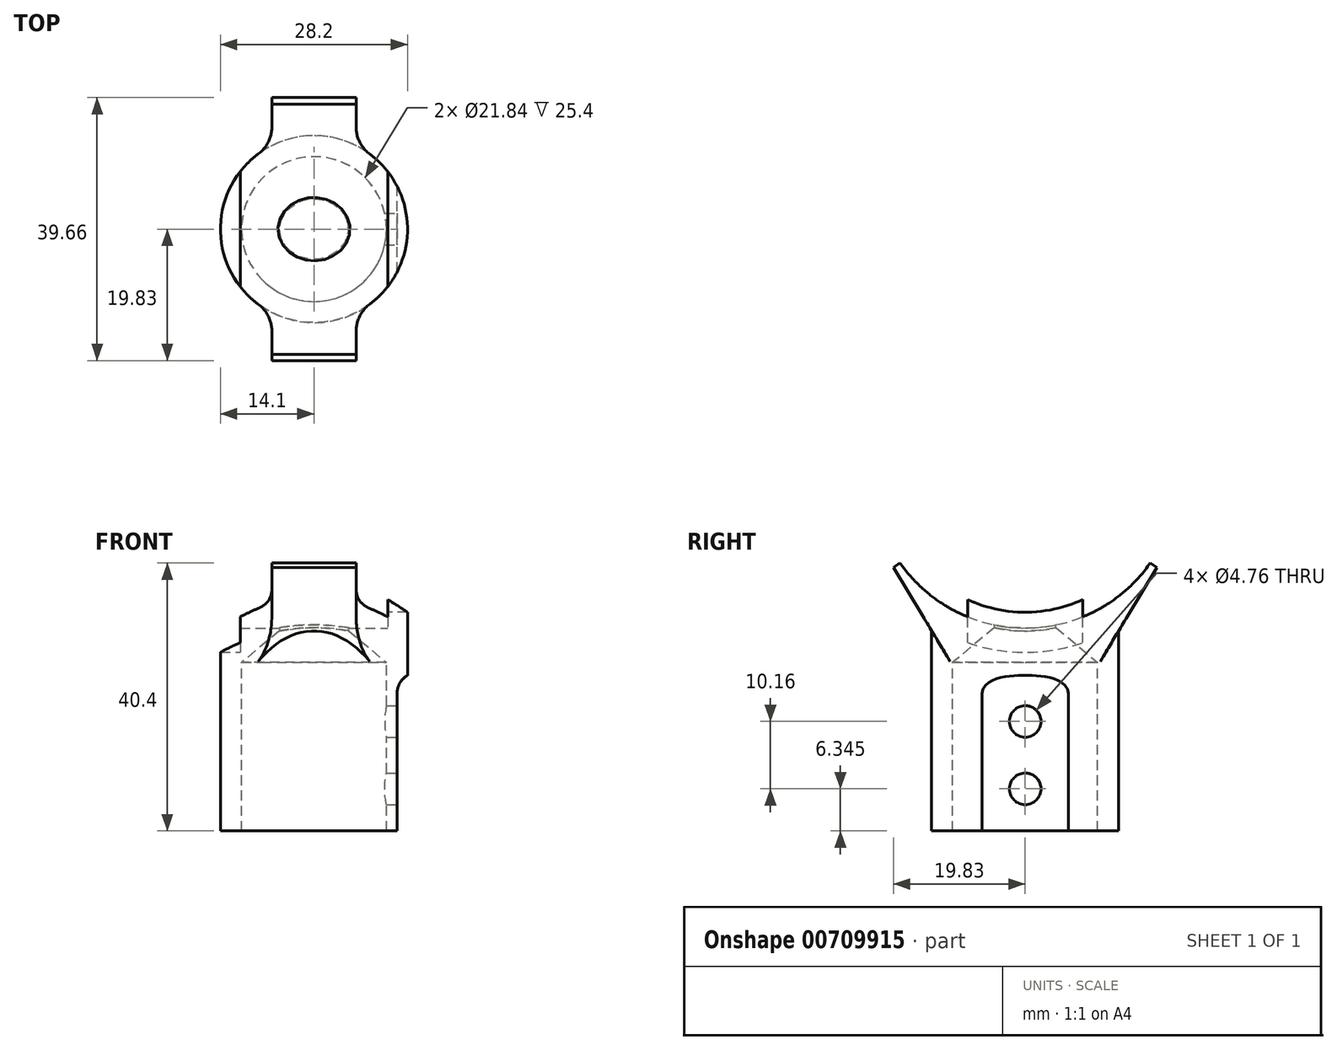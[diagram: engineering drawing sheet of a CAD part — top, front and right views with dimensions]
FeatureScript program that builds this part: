
annotation { "Feature Type Name" : "Feature", "Feature Type Description" : "" }
export const myFeature = defineFeature(function(context is Context, id is Id, definition is map)
    precondition{}
    {
        {
            var Q0;
            Q0=qCreatedBy(makeId("Front.planeOp"),FACE);
            var sketch = newSketch(context, id + "F0", { "sketchPlane" : qUnion([Q0])});
            skLineSegment(sketch, "E0", {"start": v(0, 0) * mm, "end": v(-10.92, -9.16) * mm});
            skLineSegment(sketch, "E1", {"start": v(-10.92, -9.16) * mm, "end": v(-10.92, -34.56) * mm});
            skLineSegment(sketch, "E2", {"start": v(0, 0) * mm, "end": v(0, -71.28) * mm, "construction": true});
            skLineSegment(sketch, "E3", {"start": v(-10.92, -34.56) * mm, "end": v(-14.1, -34.56) * mm});
            skLineSegment(sketch, "E4", {"start": v(-14.1, -34.56) * mm, "end": v(-14.1, 9.52) * mm});
            skLineSegment(sketch, "E5", {"start": v(-14.1, 9.52) * mm, "end": v(0, 9.52) * mm});
            skLineSegment(sketch, "E6", {"start": v(0, 9.52) * mm, "end": v(0, 0) * mm});
            skSolve(sketch);
        }
        {
            var Q0;
            Q0=makeQuery(id+"F0.imprint","IMPRINT",FACE,{"disambiguationData":[TD([[makeQuery(id+"F0.imprint","IMPRINT",EDGE,{"derivedFrom":sQuery(id+"F0.wireOp",EDGE,"E0")}),-1.0]])]});
            var Q1;
            Q1=sQuery(id+"F0.wireOp",EDGE,"E2");
            revolve(context, id + "F1", {"entities" : qUnion([Q0]), "axis" : qUnion([Q1]), "revolveType" : RevolveType.FULL, "surfaceOperationType" : NewSurfaceOperationType.NEW});
        }
        {
            var Q0;
            Q0=makeQuery(id+"F1.opRevolve","SWEPT_EDGE",EDGE,{"disambiguationData":[OSD([sQuery(id+"F0.wireOp",EDGE,"E4"),sQuery(id+"F0.wireOp",EDGE,"E5")])]});
            fillet(context, id + "F2", {"entities" : qUnion([Q0]), "radius" : 2.38 * mm, "tangentPropagation" : true, "allowEdgeOverflow" : false});
        }
        {
            var Q0;
            Q0=qCreatedBy(makeId("Front.planeOp"),FACE);
            var sketch = newSketch(context, id + "F3", { "sketchPlane" : qUnion([Q0])});
            skLineSegment(sketch, "E7", {"start": v(10.92, -10.67) * mm, "end": v(10.92, -36.07) * mm});
            skLineSegment(sketch, "E8", {"start": v(-10.92, -36.07) * mm, "end": v(-10.92, -10.67) * mm});
            skLineSegment(sketch, "E9", {"start": v(-14.1, -36.07) * mm, "end": v(-14.1, 3.17) * mm});
            skLineSegment(sketch, "E10", {"start": v(12.5, -13.84) * mm, "end": v(12.5, -38.6) * mm});
            skLineSegment(sketch, "E11", {"start": v(15.68, -10.67) * mm, "end": v(18.86, -10.67) * mm});
            skLineSegment(sketch, "E12", {"start": v(18.86, -10.67) * mm, "end": v(18.86, -38.6) * mm});
            skLineSegment(sketch, "E13", {"start": v(18.86, -38.6) * mm, "end": v(12.5, -38.6) * mm});
            skPoint(sketch, "E14.visualSharp", {"position": v(12.5, -10.67) * mm});
            skArc(sketch, "E14.filletArc", {"start": v(15.68, -10.67) * mm, "mid": v(13.44, -11.6) * mm, "end": v(12.5, -13.84) * mm});
            skSolve(sketch);
        }
        {
            var Q0;
            Q0=makeQuery(id+"F3.imprint","IMPRINT",FACE,{"disambiguationData":[TD([[makeQuery(id+"F3.imprint","IMPRINT",EDGE,{"derivedFrom":sQuery(id+"F3.wireOp",EDGE,"E10")}),1.0]])]});
            extrude(context, id + "F4", {"entities" : qUnion([Q0]), "operationType" : NewBodyOperationType.REMOVE, "depth" : 25.4 * mm, "hasSecondDirection" : true, "secondDirectionOppositeDirection" : true, "secondDirectionDepth" : 25.4 * mm, "offsetDistance" : 25.4 * mm});
        }
        {
            var Q0;
            Q0=makeQuery(id+"F4.boolean.opBoolean","COPY",FACE,{"derivedFrom":makeQuery(id+"F4.opExtrude","SWEPT_FACE",FACE,{"disambiguationData":[OSD([sQuery(id+"F3.wireOp",EDGE,"E10")])]})});
            var sketch = newSketch(context, id + "F5", { "sketchPlane" : qUnion([Q0])});
            skLineSegment(sketch, "E15", {"start": v(0, -34.56) * mm, "end": v(0, -13.84) * mm, "construction": true});
            skCircle(sketch, "E16", {"center": v(0, -18.05) * mm, "radius": 2.38 * mm});
            skCircle(sketch, "E17", {"center": v(0, -28.21) * mm, "radius": 2.38 * mm});
            skSolve(sketch);
        }
        {
            var Q0;
            Q0=makeQuery(id+"F5.imprint","IMPRINT",FACE,{"disambiguationData":[TD([[makeQuery(id+"F5.imprint","IMPRINT",EDGE,{"derivedFrom":sQuery(id+"F5.wireOp",EDGE,"E16")}),1.0]])]});
            var Q1;
            Q1=makeQuery(id+"F5.imprint","IMPRINT",FACE,{"disambiguationData":[TD([[makeQuery(id+"F5.imprint","IMPRINT",EDGE,{"derivedFrom":sQuery(id+"F5.wireOp",EDGE,"E17")}),1.0]])]});
            extrude(context, id + "F6", {"entities" : qUnion([Q0, Q1]), "operationType" : NewBodyOperationType.REMOVE, "oppositeDirection" : true, "depth" : 6.35 * mm, "offsetDistance" : 25.4 * mm});
        }
        {
            var Q0;
            Q0=qCreatedBy(makeId("Right.planeOp"),FACE);
            var sketch = newSketch(context, id + "F7", { "sketchPlane" : qUnion([Q0])});
            skLineSegment(sketch, "E18", {"start": v(-11.12, -9.33) * mm, "end": v(0, 0) * mm});
            skLineSegment(sketch, "E19", {"start": v(0, 0) * mm, "end": v(11.12, -9.33) * mm});
            skLineSegment(sketch, "E20", {"start": v(-11.12, -9.33) * mm, "end": v(-21.59, 8.08) * mm});
            skLineSegment(sketch, "E21", {"start": v(0, 0) * mm, "end": v(0, 19.05) * mm, "construction": true});
            skLineSegment(sketch, "E22.MirrorCS", {"start": v(11.12, -9.33) * mm, "end": v(21.59, 8.08) * mm});
            skLineSegment(sketch, "E23", {"start": v(-21.6, 8.08) * mm, "end": v(21.59, 8.08) * mm});
            skCircle(sketch, "E24", {"center": v(0, 19.05) * mm, "radius": 23.03 * mm, "construction": true});
            skLineSegment(sketch, "E25", {"start": v(-15.66, 8.08) * mm, "end": v(-19.83, 5.16) * mm});
            skLineSegment(sketch, "E26.MirrorCS", {"start": v(15.66, 8.08) * mm, "end": v(19.83, 5.16) * mm});
            skPoint(sketch, "E27.orphan", {"position": v(-25.04, 1.52) * mm});
            skPoint(sketch, "E28.orphan", {"position": v(25.04, 1.52) * mm});
            skLineSegment(sketch, "E29", {"start": v(-21.59, 8.08) * mm, "end": v(-15.66, 8.08) * mm});
            skSolve(sketch);
        }
        {
            var Q0;
            Q0=makeQuery(id+"F7.imprint","IMPRINT",FACE,{"disambiguationData":[TD([[makeQuery(id+"F7.imprint","IMPRINT",EDGE,{"derivedFrom":sQuery(id+"F7.wireOp",EDGE,"E18")}),1.0]])]});
            extrude(context, id + "F8", {"entities" : qUnion([Q0]), "operationType" : NewBodyOperationType.ADD, "depth" : 6.35 * mm, "offsetDistance" : 25.4 * mm, "hasSecondDirection" : true, "secondDirectionOppositeDirection" : true, "secondDirectionDepth" : 6.35 * mm});
        }
        {
            var Q0;
            Q0=qCreatedBy(makeId("Right.planeOp"),FACE);
            var sketch = newSketch(context, id + "F9", { "sketchPlane" : qUnion([Q0])});
            skCircle(sketch, "E30.0", {"center": v(0, 19.05) * mm, "radius": 23.03 * mm});
            skSolve(sketch);
        }
        {
            var Q0;
            Q0=makeQuery(id+"F9.imprint","IMPRINT",FACE,{"disambiguationData":[TD([[makeQuery(id+"F9.imprint","IMPRINT",EDGE,{"derivedFrom":sQuery(id+"F9.wireOp",EDGE,"E30.0")}),1.0]])]});
            extrude(context, id + "F10", {"entities" : qUnion([Q0]), "operationType" : NewBodyOperationType.REMOVE, "oppositeDirection" : true, "depth" : 25.4 * mm, "offsetDistance" : 25.4 * mm, "hasSecondDirection" : true, "secondDirectionOppositeDirection" : false, "secondDirectionDepth" : 11.1 * mm});
        }
        {
            var Q0;
            Q0=makeQuery(id+"F8.boolean.opBoolean","INTERSECT",EDGE,{"disambiguationData":[OD(0.0)],"derivedFrom":[makeQuery(id+"F1.opRevolve","SWEPT_FACE",FACE,{"disambiguationData":[OSD([sQuery(id+"F0.wireOp",EDGE,"E4")])]}),makeQuery(id+"F8.opExtrude","CAP_FACE",FACE,{"disambiguationData":[OSD([sQuery(id+"F7.wireOp",EDGE,"E18"),sQuery(id+"F7.wireOp",EDGE,"E19"),sQuery(id+"F7.wireOp",EDGE,"E20"),sQuery(id+"F7.wireOp",EDGE,"E22.MirrorCS"),sQuery(id+"F7.wireOp",EDGE,"E23")])],"isStart":false})]});
            var Q1;
            Q1=makeQuery(id+"F8.boolean.opBoolean","INTERSECT",EDGE,{"disambiguationData":[OD(1.0)],"derivedFrom":[makeQuery(id+"F1.opRevolve","SWEPT_FACE",FACE,{"disambiguationData":[OSD([sQuery(id+"F0.wireOp",EDGE,"E4")])]}),makeQuery(id+"F8.opExtrude","CAP_FACE",FACE,{"disambiguationData":[OSD([sQuery(id+"F7.wireOp",EDGE,"E18"),sQuery(id+"F7.wireOp",EDGE,"E19"),sQuery(id+"F7.wireOp",EDGE,"E20"),sQuery(id+"F7.wireOp",EDGE,"E22.MirrorCS"),sQuery(id+"F7.wireOp",EDGE,"E23")])],"isStart":false})]});
            var Q2;
            Q2=makeQuery(id+"F8.boolean.opBoolean","INTERSECT",EDGE,{"disambiguationData":[OD(1.0)],"derivedFrom":[makeQuery(id+"F1.opRevolve","SWEPT_FACE",FACE,{"disambiguationData":[OSD([sQuery(id+"F0.wireOp",EDGE,"E4")])]}),makeQuery(id+"F8.opExtrude","CAP_FACE",FACE,{"disambiguationData":[OSD([sQuery(id+"F7.wireOp",EDGE,"E18"),sQuery(id+"F7.wireOp",EDGE,"E19"),sQuery(id+"F7.wireOp",EDGE,"E20"),sQuery(id+"F7.wireOp",EDGE,"E22.MirrorCS"),sQuery(id+"F7.wireOp",EDGE,"E23")])],"isStart":true})]});
            var Q3;
            Q3=makeQuery(id+"F8.boolean.opBoolean","INTERSECT",EDGE,{"disambiguationData":[OD(0.0)],"derivedFrom":[makeQuery(id+"F1.opRevolve","SWEPT_FACE",FACE,{"disambiguationData":[OSD([sQuery(id+"F0.wireOp",EDGE,"E4")])]}),makeQuery(id+"F8.opExtrude","CAP_FACE",FACE,{"disambiguationData":[OSD([sQuery(id+"F7.wireOp",EDGE,"E18"),sQuery(id+"F7.wireOp",EDGE,"E19"),sQuery(id+"F7.wireOp",EDGE,"E20"),sQuery(id+"F7.wireOp",EDGE,"E22.MirrorCS"),sQuery(id+"F7.wireOp",EDGE,"E23")])],"isStart":true})]});
            fillet(context, id + "F11", {"entities" : qUnion([Q0, Q1, Q2, Q3]), "radius" : 5.08 * mm, "tangentPropagation" : true, "allowEdgeOverflow" : false});
        }
        {
            var Q0;
            Q0=qCreatedBy(makeId("Right.planeOp"),FACE);
            var sketch = newSketch(context, id + "F12", { "sketchPlane" : qUnion([Q0])});
            skCircle(sketch, "E31", {"center": v(0, 19.05) * mm, "radius": 20.64 * mm});
            skSolve(sketch);
        }
        {
            var Q0;
            Q0=makeQuery(id+"F12.imprint","IMPRINT",FACE,{"disambiguationData":[TD([[makeQuery(id+"F12.imprint","IMPRINT",EDGE,{"derivedFrom":sQuery(id+"F12.wireOp",EDGE,"E31")}),1.0]])]});
            extrude(context, id + "F13", {"entities" : qUnion([Q0]), "operationType" : NewBodyOperationType.REMOVE, "depth" : 25.4 * mm, "offsetDistance" : 25.4 * mm});
        }
        {
            var Q0;
            Q0=qCreatedBy(makeId("Right.planeOp"),FACE);
            cPlane(context, id + "F14", {"entities" : qUnion([Q0]), "cplaneType" : CPlaneType.OFFSET, "offset" : 11.1 * mm, "oppositeDirection" : true, "width" : 152.4 * mm, "height" : 152.4 * mm});
        }
        {
            var Q0;
            Q0=qCreatedBy(id+"F14.planeOp",FACE);
            var sketch = newSketch(context, id + "F15", { "sketchPlane" : qUnion([Q0])});
            skPoint(sketch, "E32.0", {"position": v(0, 19.05) * mm});
            skCircle(sketch, "E33", {"center": v(0, 19.05) * mm, "radius": 26.67 * mm});
            skSolve(sketch);
        }
        {
            var Q0;
            Q0=makeQuery(id+"F15.imprint","IMPRINT",FACE,{"disambiguationData":[TD([[makeQuery(id+"F15.imprint","IMPRINT",EDGE,{"derivedFrom":sQuery(id+"F15.wireOp",EDGE,"E33")}),1.0]])]});
            extrude(context, id + "F16", {"entities" : qUnion([Q0]), "operationType" : NewBodyOperationType.REMOVE, "oppositeDirection" : true, "depth" : 25.4 * mm, "offsetDistance" : 25.4 * mm});
        }
        {
            var Q0;
            Q0=makeQuery(id+"F10.boolean.opBoolean","INTERSECT",EDGE,{"derivedFrom":[makeQuery(id+"F1.opRevolve","SWEPT_FACE",FACE,{"disambiguationData":[OSD([sQuery(id+"F0.wireOp",EDGE,"E0")])]}),makeQuery(id+"F10.opExtrude","SWEPT_FACE",FACE,{"disambiguationData":[OSD([sQuery(id+"F9.wireOp",EDGE,"E30.0")])]})]});
            fillet(context, id + "F17", {"entities" : qUnion([Q0]), "radius" : 0.25 * mm, "tangentPropagation" : true, "allowEdgeOverflow" : false});
        }
        {
            var Q0;
            Q0=makeQuery(id+"F1.opRevolve","SWEPT_BODY",BODY,{"disambiguationData":[OSD([sQuery(id+"F0.wireOp",EDGE,"E0"),sQuery(id+"F0.wireOp",EDGE,"E1"),sQuery(id+"F0.wireOp",EDGE,"E3"),sQuery(id+"F0.wireOp",EDGE,"E4"),sQuery(id+"F0.wireOp",EDGE,"E5"),sQuery(id+"F0.wireOp",EDGE,"E6")])]});
            transform(context, id + "F18", {"entities" : qUnion([Q0]), "transformType" : TransformType.TRANSLATION_3D, "dx" : 0 * mm, "dy" : 0 * mm, "dz" : 0 * mm, "makeCopy" : true});
        }
    });
